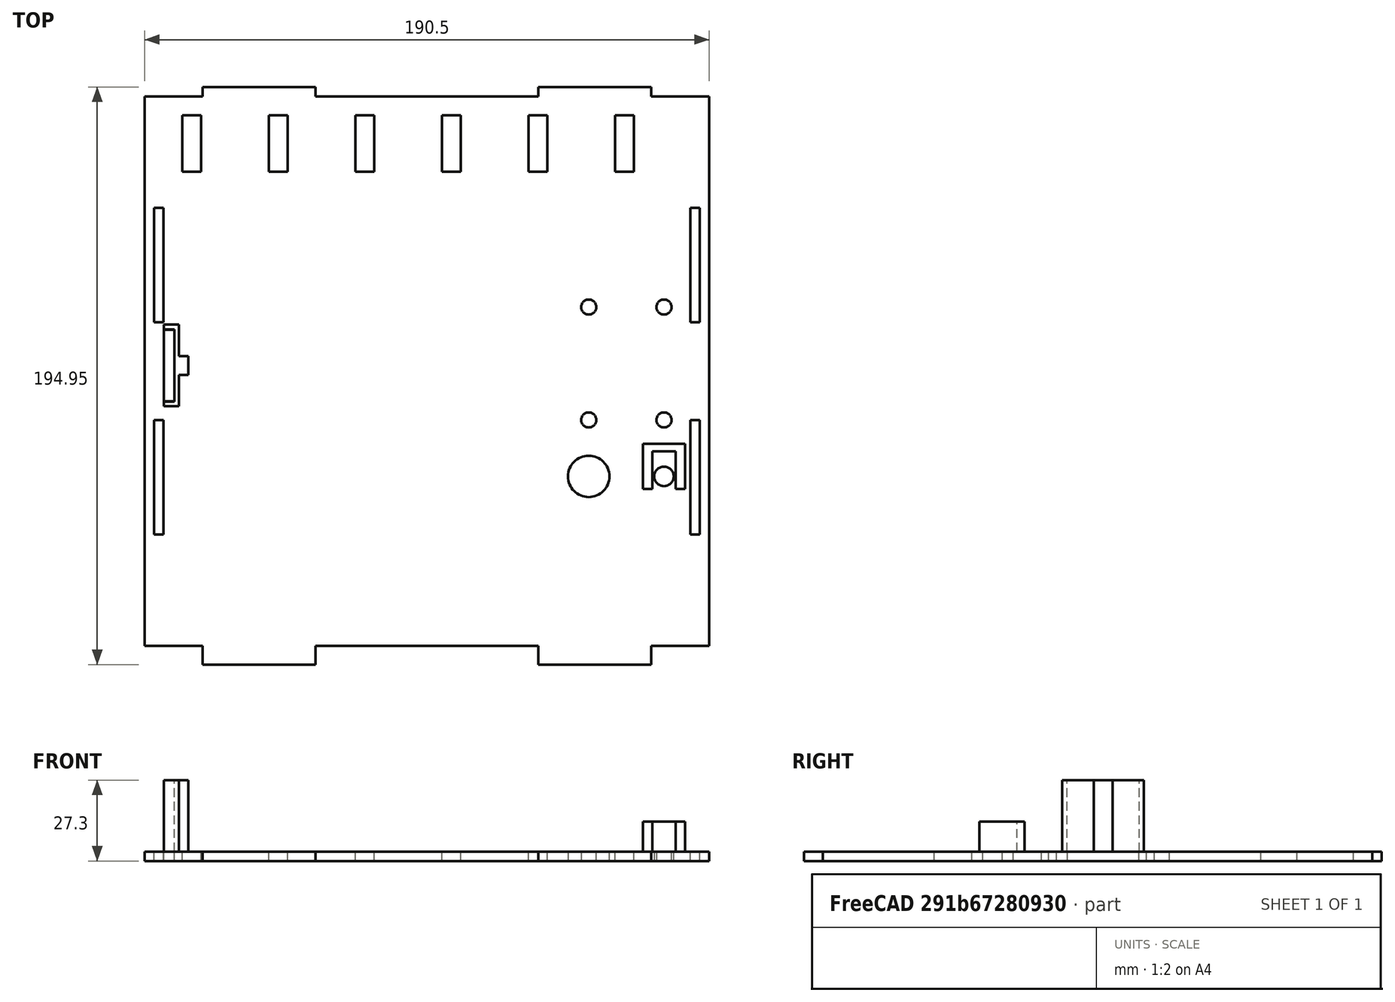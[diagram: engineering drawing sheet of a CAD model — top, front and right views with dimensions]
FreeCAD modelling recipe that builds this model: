
FCSTD DOCUMENT  (FreeCAD 0.18R4 (GitTag))
Label: fpr68k
License: All rights reserved
LicenseURL: http://en.wikipedia.org/wiki/All_rights_reserved
objects: Sketcher::SketchObject×3, PartDesign::Pad×3, PartDesign::Body×1, App::Part×1, Mesh::Feature×1
note: 10 computed .brp shape members not serialized (recipe doc carries the construction recipe); baked Part::Feature solids carry a one-line shape summary decoded from their .brp

FEATURE [Sketcher::SketchObject] Sketch
  MapMode = 5
  Support = -> [XY_Plane001]
  sketch-geometry (70):
    g0: LineSegment StartX=-132.842 StartY=92.71 StartZ=0 EndX=-113.284 EndY=92.71 EndZ=0
    g1: LineSegment StartX=-113.284 StartY=92.71 StartZ=0 EndX=-113.284 EndY=95.885 EndZ=0
    g2: LineSegment StartX=-113.284 StartY=95.885 StartZ=0 EndX=-75.184 EndY=95.885 EndZ=0
    g3: LineSegment StartX=-75.184 StartY=95.885 StartZ=0 EndX=-75.184 EndY=92.71 EndZ=0
    g4: LineSegment StartX=-75.184 StartY=92.71 StartZ=0 EndX=0 EndY=92.71 EndZ=0
    g5: LineSegment StartX=0 StartY=92.71 StartZ=0 EndX=0 EndY=95.885 EndZ=0
    g6: LineSegment StartX=0 StartY=95.885 StartZ=0 EndX=38.1 EndY=95.885 EndZ=0
    g7: LineSegment StartX=38.1 StartY=95.885 StartZ=0 EndX=38.1 EndY=92.71 EndZ=0
    g8: LineSegment StartX=38.1 StartY=92.71 StartZ=0 EndX=57.658 EndY=92.71 EndZ=0
    g9: LineSegment StartX=57.658 StartY=92.71 StartZ=0 EndX=57.658 EndY=-92.71 EndZ=0
    g10: LineSegment StartX=57.658 StartY=-92.71 StartZ=0 EndX=38.1 EndY=-92.71 EndZ=0
    g11: LineSegment StartX=38.1 StartY=-92.71 StartZ=0 EndX=38.1 EndY=-99.06 EndZ=0
    g12: LineSegment StartX=38.1 StartY=-99.06 StartZ=0 EndX=7.1e-15 EndY=-99.06 EndZ=0
    g13: LineSegment StartX=5.6e-15 StartY=-99.06 StartZ=0 EndX=5.6e-15 EndY=-92.71 EndZ=0
    g14: LineSegment StartX=5.6e-15 StartY=-92.71 StartZ=0 EndX=-75.184 EndY=-92.71 EndZ=0
    g15: LineSegment StartX=-75.184 StartY=-92.71 StartZ=0 EndX=-75.184 EndY=-99.06 EndZ=0
    g16: LineSegment StartX=-75.184 StartY=-99.06 StartZ=0 EndX=-113.284 EndY=-99.06 EndZ=0
    g17: LineSegment StartX=-113.284 StartY=-99.06 StartZ=0 EndX=-113.284 EndY=-92.71 EndZ=0
    g18: LineSegment StartX=-113.284 StartY=-92.71 StartZ=0 EndX=-132.842 EndY=-92.71 EndZ=0
    g19: LineSegment StartX=-132.842 StartY=-92.71 StartZ=0 EndX=-132.842 EndY=92.71 EndZ=0
    g20: LineSegment StartX=-129.718 StartY=55.118 StartZ=0 EndX=-126.441 EndY=55.118 EndZ=0
    g21: LineSegment StartX=-126.441 StartY=55.118 StartZ=0 EndX=-126.441 EndY=16.51 EndZ=0
    g22: LineSegment StartX=-126.441 StartY=16.51 StartZ=0 EndX=-129.718 EndY=16.51 EndZ=0
    g23: LineSegment StartX=-129.718 StartY=16.51 StartZ=0 EndX=-129.718 EndY=55.118 EndZ=0
    g24: LineSegment StartX=51.2572 StartY=55.118 StartZ=0 EndX=54.5338 EndY=55.118 EndZ=0
    g25: LineSegment StartX=54.5338 StartY=55.118 StartZ=0 EndX=54.5338 EndY=16.51 EndZ=0
    g26: LineSegment StartX=54.5338 StartY=16.51 StartZ=0 EndX=51.2572 EndY=16.51 EndZ=0
    g27: LineSegment StartX=51.2572 StartY=16.51 StartZ=0 EndX=51.2572 EndY=55.118 EndZ=0
    g28: LineSegment StartX=51.2572 StartY=-16.51 StartZ=0 EndX=54.5338 EndY=-16.51 EndZ=0
    g29: LineSegment StartX=54.5338 StartY=-16.51 StartZ=0 EndX=54.5338 EndY=-55.118 EndZ=0
    g30: LineSegment StartX=54.5338 StartY=-55.118 StartZ=0 EndX=51.2572 EndY=-55.118 EndZ=0
    g31: LineSegment StartX=51.2572 StartY=-55.118 StartZ=0 EndX=51.2572 EndY=-16.51 EndZ=0
    g32: LineSegment StartX=-129.718 StartY=-16.51 StartZ=0 EndX=-126.441 EndY=-16.51 EndZ=0
    g33: LineSegment StartX=-126.441 StartY=-16.51 StartZ=0 EndX=-126.441 EndY=-55.118 EndZ=0
    g34: LineSegment StartX=-126.441 StartY=-55.118 StartZ=0 EndX=-129.718 EndY=-55.118 EndZ=0
    g35: LineSegment StartX=-129.718 StartY=-55.118 StartZ=0 EndX=-129.718 EndY=-16.51 EndZ=0
    g36: LineSegment StartX=-126.416 StartY=13.97 StartZ=0 EndX=-122.809 EndY=13.97 EndZ=0
    g37: LineSegment StartX=-122.809 StartY=13.97 StartZ=0 EndX=-122.809 EndY=-10.16 EndZ=0
    g38: LineSegment StartX=-122.809 StartY=-10.16 StartZ=0 EndX=-126.416 EndY=-10.16 EndZ=0
    g39: LineSegment StartX=-126.416 StartY=-10.16 StartZ=0 EndX=-126.416 EndY=13.97 EndZ=0
    g40: Circle CenterX=42.418 CenterY=-35.56 CenterZ=0 NormalX=0 NormalY=0 NormalZ=1 AngleXU=0 Radius=3.302
    g41: LineSegment StartX=-120.142 StartY=86.36 StartZ=0 EndX=-113.792 EndY=86.36 EndZ=0
    g42: LineSegment StartX=-113.792 StartY=86.36 StartZ=0 EndX=-113.792 EndY=67.31 EndZ=0
    g43: LineSegment StartX=-113.792 StartY=67.31 StartZ=0 EndX=-120.142 EndY=67.31 EndZ=0
    g44: LineSegment StartX=-120.142 StartY=67.31 StartZ=0 EndX=-120.142 EndY=86.36 EndZ=0
    g45: LineSegment StartX=-84.582 StartY=86.36 StartZ=0 EndX=-90.932 EndY=86.36 EndZ=0
    g46: LineSegment StartX=-90.932 StartY=86.36 StartZ=0 EndX=-90.932 EndY=67.31 EndZ=0
    g47: LineSegment StartX=-90.932 StartY=67.31 StartZ=0 EndX=-84.582 EndY=67.31 EndZ=0
    g48: LineSegment StartX=-84.582 StartY=67.31 StartZ=0 EndX=-84.582 EndY=86.36 EndZ=0
    g49: LineSegment StartX=-61.722 StartY=86.36 StartZ=0 EndX=-55.372 EndY=86.36 EndZ=0
    g50: LineSegment StartX=-55.372 StartY=86.36 StartZ=0 EndX=-55.372 EndY=67.31 EndZ=0
    g51: LineSegment StartX=-55.372 StartY=67.31 StartZ=0 EndX=-61.722 EndY=67.31 EndZ=0
    g52: LineSegment StartX=-61.722 StartY=67.31 StartZ=0 EndX=-61.722 EndY=86.36 EndZ=0
    g53: LineSegment StartX=-32.512 StartY=86.36 StartZ=0 EndX=-26.162 EndY=86.36 EndZ=0
    g54: LineSegment StartX=-26.162 StartY=86.36 StartZ=0 EndX=-26.162 EndY=67.31 EndZ=0
    g55: LineSegment StartX=-26.162 StartY=67.31 StartZ=0 EndX=-32.512 EndY=67.31 EndZ=0
    g56: LineSegment StartX=-32.512 StartY=67.31 StartZ=0 EndX=-32.512 EndY=86.36 EndZ=0
    g57: LineSegment StartX=-3.302 StartY=86.36 StartZ=0 EndX=3.048 EndY=86.36 EndZ=0
    g58: LineSegment StartX=3.048 StartY=86.36 StartZ=0 EndX=3.048 EndY=67.31 EndZ=0
    g59: LineSegment StartX=3.048 StartY=67.31 StartZ=0 EndX=-3.302 EndY=67.31 EndZ=0
    g60: LineSegment StartX=-3.302 StartY=67.31 StartZ=0 EndX=-3.302 EndY=86.36 EndZ=0
    g61: LineSegment StartX=25.908 StartY=86.36 StartZ=0 EndX=32.258 EndY=86.36 EndZ=0
    g62: LineSegment StartX=32.258 StartY=86.36 StartZ=0 EndX=32.258 EndY=67.31 EndZ=0
    g63: LineSegment StartX=32.258 StartY=67.31 StartZ=0 EndX=25.908 EndY=67.31 EndZ=0
    g64: LineSegment StartX=25.908 StartY=67.31 StartZ=0 EndX=25.908 EndY=86.36 EndZ=0
    g65: Circle CenterX=42.418 CenterY=21.59 CenterZ=0 NormalX=0 NormalY=0 NormalZ=1 AngleXU=0 Radius=2.54
    g66: Circle CenterX=17.018 CenterY=21.59 CenterZ=0 NormalX=0 NormalY=0 NormalZ=1 AngleXU=0 Radius=2.54
    g67: Circle CenterX=17.018 CenterY=-16.51 CenterZ=0 NormalX=0 NormalY=0 NormalZ=1 AngleXU=0 Radius=2.54
    g68: Circle CenterX=42.418 CenterY=-16.51 CenterZ=0 NormalX=0 NormalY=0 NormalZ=1 AngleXU=0 Radius=2.54
    g69: Circle CenterX=17.018 CenterY=-35.56 CenterZ=0 NormalX=0 NormalY=0 NormalZ=1 AngleXU=0 Radius=6.985
  constraints (208):
    c: Horizontal(g0)
    c: Coincident(g0,g1)
    c: Vertical(g1)
    c: Coincident(g1,g2)
    c: Horizontal(g2)
    c: Coincident(g2,g3)
    c: Coincident(g3,g4)
    c: Horizontal(g4)
    c: Coincident(g4,g5)
    c: PointOnObject(g5,g-2)
    c: Vertical(g5)
    c: Coincident(g5,g6)
    c: Coincident(g6,g7)
    c: Coincident(g7,g8)
    c: Horizontal(g8)
    c: Coincident(g8,g9)
    c: Coincident(g9,g10)
    c: Horizontal(g10)
    c: Coincident(g10,g11)
    c: Vertical(g11)
    c: Coincident(g11,g12)
    c: Coincident(g12,g13)
    c: Coincident(g13,g14)
    c: Horizontal(g14)
    c: Coincident(g14,g15)
    c: Coincident(g15,g16)
    c: Horizontal(g16)
    c: Coincident(g16,g17)
    c: Coincident(g17,g18)
    c: Horizontal(g18)
    c: Coincident(g18,g19)
    c: Coincident(g19,g0)
    c: Symmetric(g0,g18,g-1)
    c: Symmetric(g8,g9,g-1)
    c: Equal(g9,g19)
    c: DistanceY(g9,g8) = 185.42
    c: Perpendicular(g3,g2)
    c: Perpendicular(g7,g6)
    c: Perpendicular(g13,g12)
    c: Perpendicular(g15,g14)
    c: Equal(g17,g15)
    c: Equal(g15,g13)
    c: Equal(g13,g11)
    c: Equal(g10,g18)
    c: Equal(g18,g0)
    c: Equal(g0,g8)
    c: Equal(g7,g5)
    c: Equal(g5,g3)
    c: Equal(g3,g1)
    c: DistanceX(g10,g9) = 19.558
    c: Equal(g12,g16)
    c: Equal(g16,g2)
    c: Equal(g2,g6)
    c: Equal(g4,g14)
    c: DistanceX(g12,g11) = 38.1
    c: DistanceX(g3,g4) = 75.184
    c: DistanceY(g7,g6) = 3.175
    c: DistanceY(g16,g17) = 6.35
    c: Coincident(g20,g21)
    c: Coincident(g21,g22)
    c: Coincident(g22,g23)
    c: Coincident(g23,g20)
    c: Horizontal(g20)
    c: Horizontal(g22)
    c: Vertical(g21)
    c: Vertical(g23)
    c: DistanceY(g20,g0) = 37.592
    c: DistanceX(g0,g20) = 3.1242
    c: Coincident(g24,g25)
    c: Coincident(g25,g26)
    c: Coincident(g26,g27)
    c: Coincident(g27,g24)
    c: Horizontal(g24)
    c: Horizontal(g26)
    c: Vertical(g25)
    c: Vertical(g27)
    c: DistanceY(g24,g8) = 37.592
    c: DistanceX(g24,g8) = 3.1242
    c: Coincident(g28,g29)
    c: Coincident(g29,g30)
    c: Coincident(g30,g31)
    c: Coincident(g31,g28)
    c: Horizontal(g28)
    c: Horizontal(g30)
    c: Vertical(g29)
    c: Vertical(g31)
    c: DistanceY(g9,g29) = 37.592
    c: DistanceX(g29,g9) = 3.1242
    c: Coincident(g32,g33)
    c: Coincident(g33,g34)
    c: Coincident(g34,g35)
    c: Coincident(g35,g32)
    c: Horizontal(g32)
    c: Horizontal(g34)
    c: Vertical(g33)
    c: Vertical(g35)
    c: DistanceY(g18,g34) = 37.592
    c: DistanceX(g18,g34) = 3.1242
    c: Equal(g33,g31)
    c: Equal(g31,g27)
    c: Equal(g27,g21)
    c: DistanceY(g33,g32) = 38.608
    c: Equal(g28,g26)
    c: Equal(g26,g22)
    c: Equal(g22,g32)
    c: DistanceX(g28,g28) = 3.2766
    c: Coincident(g36,g37)
    c: Coincident(g37,g38)
    c: Coincident(g38,g39)
    c: Coincident(g39,g36)
    c: Horizontal(g36)
    c: Horizontal(g38)
    c: Vertical(g37)
    c: Vertical(g39)
    c: DistanceY(g18,g38) = 82.55
    c: DistanceX(g18,g38) = 6.4262
    c: DistanceY(g37,g36) = 24.13
    c: DistanceX(g38,g37) = 3.6068
    c: Diameter(g40) = 6.604
    c: DistanceY(g9,g40) = 57.15
    c: DistanceX(g40,g9) = 15.24
    c: Coincident(g41,g42)
    c: Coincident(g42,g43)
    c: Coincident(g43,g44)
    c: Coincident(g44,g41)
    c: Horizontal(g41)
    c: Horizontal(g43)
    c: Vertical(g42)
    c: Vertical(g44)
    c: Coincident(g45,g46)
    c: Coincident(g46,g47)
    c: Coincident(g47,g48)
    c: Coincident(g48,g45)
    c: Horizontal(g45)
    c: Horizontal(g47)
    c: Vertical(g46)
    c: Vertical(g48)
    c: Coincident(g49,g50)
    c: Coincident(g50,g51)
    c: Coincident(g51,g52)
    c: Coincident(g52,g49)
    c: Horizontal(g49)
    c: Horizontal(g51)
    c: Vertical(g50)
    c: Vertical(g52)
    c: Coincident(g53,g54)
    c: Coincident(g54,g55)
    c: Coincident(g55,g56)
    c: Coincident(g56,g53)
    c: Horizontal(g53)
    c: Horizontal(g55)
    c: Vertical(g54)
    c: Vertical(g56)
    c: Coincident(g57,g58)
    c: Coincident(g58,g59)
    c: Coincident(g59,g60)
    c: Coincident(g60,g57)
    c: Horizontal(g57)
    c: Horizontal(g59)
    c: Vertical(g58)
    c: Vertical(g60)
    c: Coincident(g61,g62)
    c: Coincident(g62,g63)
    c: Coincident(g63,g64)
    c: Coincident(g64,g61)
    c: Horizontal(g61)
    c: Horizontal(g63)
    c: Vertical(g62)
    c: Vertical(g64)
    c: DistanceX(g61,g8) = 31.75
    c: DistanceY(g61,g8) = 6.35
    c: DistanceX(g53,g57) = 29.21
    c: DistanceX(g57,g61) = 29.21
    c: DistanceX(g49,g53) = 29.21
    c: DistanceX(g45,g49) = 29.21
    c: DistanceX(g41,g45) = 29.21
    c: Equal(g61,g57)
    c: Equal(g57,g53)
    c: Equal(g53,g49)
    c: Equal(g49,g45)
    c: Equal(g45,g41)
    c: DistanceX(g61,g61) = 6.35
    c: DistanceY(g57,g61) = 0
    c: DistanceY(g53,g61) = 0
    c: DistanceY(g49,g61) = 0
    c: DistanceY(g45,g61) = 0
    c: DistanceY(g41,g61) = 0
    c: Equal(g64,g60)
    c: Equal(g60,g56)
    c: Equal(g56,g52)
    c: Equal(g52,g46)
    c: Equal(g46,g44)
    c: DistanceY(g63,g61) = 19.05
    c: Diameter(g65) = 5.08
    c: Equal(g65,g66)
    c: Equal(g65,g67)
    c: Equal(g65,g68)
    c: DistanceX(g66,g65) = 25.4
    c: DistanceX(g67,g68) = 25.4
    c: DistanceY(g67,g66) = 38.1
    c: DistanceY(g68,g65) = 38.1
    c: DistanceY(g66,g65) = 0
    c: DistanceX(g40,g68) = 0
    c: DistanceY(g40,g68) = 19.05
    c: DistanceX(g67,g66) = 0
    c: Diameter(g69) = 13.97
    c: DistanceX(g69,g67) = 0
    c: DistanceY(g40,g69) = 0
FEATURE [Sketcher::SketchObject] Sketch001
  MapMode = 5
  Placement = pos=(0,0,3.175) rot=(0,0,1;0rad)
  sketch-geometry (12):
    g0: LineSegment StartX=-126.413 StartY=14.097 StartZ=0 EndX=-122.806 EndY=14.097 EndZ=0
    g1: LineSegment StartX=-122.806 StartY=14.097 StartZ=0 EndX=-122.806 EndY=-10.287 EndZ=0
    g2: LineSegment StartX=-122.806 StartY=-10.287 StartZ=0 EndX=-126.413 EndY=-10.287 EndZ=0
    g3: LineSegment StartX=-126.413 StartY=-10.287 StartZ=0 EndX=-126.413 EndY=-11.8745 EndZ=0
    g4: LineSegment StartX=-126.413 StartY=-11.8745 StartZ=0 EndX=-121.27 EndY=-11.8745 EndZ=0
    g5: LineSegment StartX=-121.27 StartY=-11.8745 StartZ=0 EndX=-121.27 EndY=-1.27 EndZ=0
    g6: LineSegment StartX=-121.27 StartY=-1.27 StartZ=0 EndX=-118.095 EndY=-1.27 EndZ=0
    g7: LineSegment StartX=-118.095 StartY=-1.27 StartZ=0 EndX=-118.095 EndY=5.08 EndZ=0
    g8: LineSegment StartX=-118.095 StartY=5.08 StartZ=0 EndX=-121.27 EndY=5.08 EndZ=0
    g9: LineSegment StartX=-121.27 StartY=5.08 StartZ=0 EndX=-121.27 EndY=15.6845 EndZ=0
    g10: LineSegment StartX=-121.27 StartY=15.6845 StartZ=0 EndX=-126.413 EndY=15.6845 EndZ=0
    g11: LineSegment StartX=-126.413 StartY=15.6845 StartZ=0 EndX=-126.413 EndY=14.097 EndZ=0
  constraints (36):
    c: Horizontal(g0)
    c: Coincident(g0,g1)
    c: Vertical(g1)
    c: Coincident(g1,g2)
    c: Horizontal(g2)
    c: Coincident(g2,g3)
    c: Vertical(g3)
    c: Coincident(g3,g4)
    c: Horizontal(g4)
    c: Coincident(g4,g5)
    c: Vertical(g5)
    c: Coincident(g5,g6)
    c: Coincident(g6,g7)
    c: Coincident(g7,g8)
    c: Coincident(g8,g9)
    c: Vertical(g9)
    c: Coincident(g9,g10)
    c: Coincident(g10,g11)
    c: Coincident(g11,g0)
    c: Perpendicular(g11,g0)
    c: Perpendicular(g10,g11)
    c: Perpendicular(g8,g9)
    c: Perpendicular(g6,g7)
    c: Equal(g11,g3)
    c: Equal(g2,g0)
    c: Equal(g10,g4)
    c: Equal(g9,g5)
    c: Equal(g8,g6)
    c: DistanceY(g6,g7) = 6.35
    c: DistanceY(g1,g0) = 24.384
    c: DistanceX(g10,g9) = 5.1435
    c: DistanceY(g0,g10) = 1.5875
    c: DistanceX(g5,g6) = 3.175
    c: DistanceX(g2,g1) = 3.6068
    c: DistanceX(g7,g-1) = 118.095
    c: DistanceY(g-1,g7) = 5.08
FEATURE [Sketcher::SketchObject] Sketch002
  MapMode = 5
  Placement = pos=(0,-11.8745,3.175) rot=(1,0,0;0rad)
  sketch-geometry (8):
    g0: LineSegment StartX=38.5318 StartY=-27.94 StartZ=0 EndX=35.3568 EndY=-27.94 EndZ=0
    g1: LineSegment StartX=35.3568 StartY=-27.94 StartZ=0 EndX=35.3568 EndY=-12.7 EndZ=0
    g2: LineSegment StartX=35.3568 StartY=-12.7 StartZ=0 EndX=49.5808 EndY=-12.7 EndZ=0
    g3: LineSegment StartX=49.5808 StartY=-12.7 StartZ=0 EndX=49.5808 EndY=-27.94 EndZ=0
    g4: LineSegment StartX=49.5808 StartY=-27.94 StartZ=0 EndX=46.4058 EndY=-27.94 EndZ=0
    g5: LineSegment StartX=46.4058 StartY=-27.94 StartZ=0 EndX=46.4058 EndY=-15.24 EndZ=0
    g6: LineSegment StartX=46.4058 StartY=-15.24 StartZ=0 EndX=38.5318 EndY=-15.24 EndZ=0
    g7: LineSegment StartX=38.5318 StartY=-15.24 StartZ=0 EndX=38.5318 EndY=-27.94 EndZ=0
  constraints (24):
    c: Coincident(g0,g1)
    c: Vertical(g1)
    c: Coincident(g1,g2)
    c: Horizontal(g2)
    c: Coincident(g2,g3)
    c: Vertical(g3)
    c: Coincident(g3,g4)
    c: Coincident(g4,g5)
    c: Vertical(g5)
    c: Coincident(g5,g6)
    c: Horizontal(g6)
    c: Coincident(g6,g7)
    c: Coincident(g7,g0)
    c: Vertical(g7)
    c: Perpendicular(g0,g7)
    c: DistanceY(g0,g6) = 12.7
    c: DistanceY(g0,g1) = 15.24
    c: DistanceX(g6,g5) = 7.874
    c: DistanceX(g0,g0) = 3.175
    c: Equal(g1,g3)
    c: Equal(g7,g5)
    c: Equal(g0,g4)
    c: DistanceX(g-1,g1) = 35.3568
    c: DistanceY(g1,g-1) = 12.7
FEATURE [PartDesign::Pad] Pad
  Length = 3.175
  Length2 = 99.9998
  Profile = -> Sketch
  Type = 0
FEATURE [PartDesign::Pad] Pad001
  BaseFeature = -> Pad
  Length = 24.13
  Length2 = 99.9998
  Profile = -> Sketch001
  Type = 0
FEATURE [PartDesign::Pad] Pad002
  BaseFeature = -> Pad001
  Length = 10.16
  Length2 = 99.9998
  Profile = -> Sketch002
  Type = 0
FEATURE [PartDesign::Body] Body
  Group = -> [Sketch,Sketch001,Sketch002,Pad,Pad001,Pad002]
  Origin = -> Origin001
  Tip = -> Pad002
FEATURE [App::Part] Part
  Group = -> [Body]
  Origin = -> Origin
FEATURE [Mesh::Feature] Mesh  label="fpr68k"
